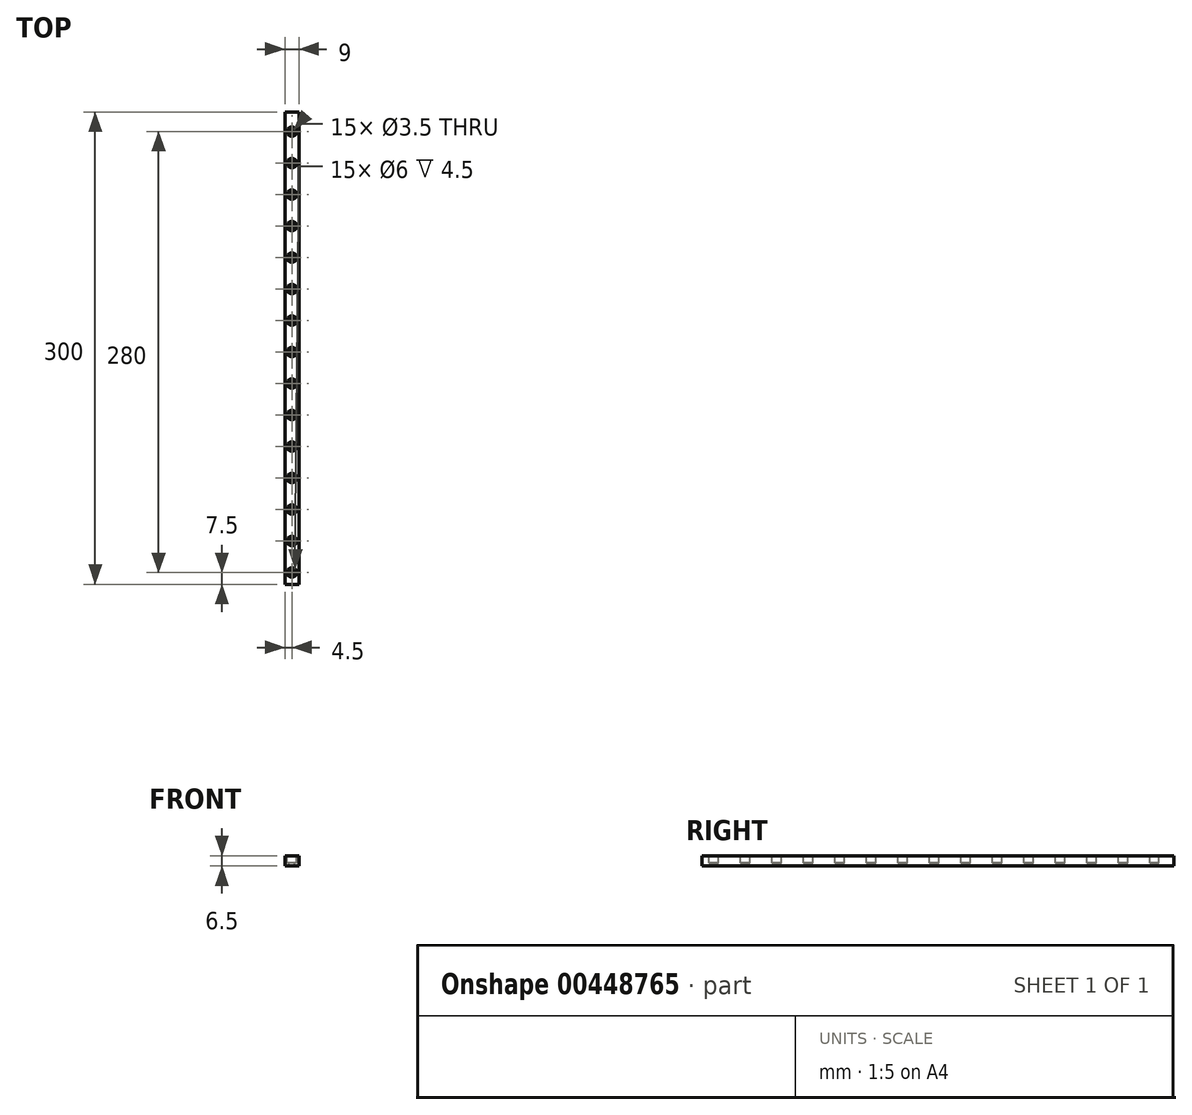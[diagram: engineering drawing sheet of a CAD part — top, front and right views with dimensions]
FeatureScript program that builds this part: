
annotation { "Feature Type Name" : "Feature", "Feature Type Description" : "" }
export const myFeature = defineFeature(function(context is Context, id is Id, definition is map)
    precondition{}
    {
        {
            var Q0;
            Q0=qCreatedBy(makeId("Front.planeOp"),FACE);
            var sketch = newSketch(context, id + "F0", { "sketchPlane" : qUnion([Q0])});
            skLineSegment(sketch, "E0.bottom", {"start": v(0, 0) * mm, "end": v(9, 0) * mm});
            skLineSegment(sketch, "E0.top", {"start": v(0, 6.5) * mm, "end": v(9, 6.5) * mm});
            skLineSegment(sketch, "E0.left", {"start": v(0, 0) * mm, "end": v(0, 6.5) * mm});
            skLineSegment(sketch, "E0.right", {"start": v(9, 0) * mm, "end": v(9, 6.5) * mm});
            skSolve(sketch);
        }
        {
            var Q0;
            Q0=qSketchRegion(id+"F0",true);
            extrude(context, id + "F1", {"entities" : qUnion([Q0]), "depth" : 300 * mm});
        }
        {
            var Q0;
            Q0=makeQuery(id+"F1.opExtrude","SWEPT_FACE",FACE,{"disambiguationData":[OSD([sQuery(id+"F0.wireOp",EDGE,"E0.top")])]});
            var sketch = newSketch(context, id + "F2", { "sketchPlane" : qUnion([Q0])});
            skPoint(sketch, "E1", {"position": v(4.5, -292.5) * mm});
            skPoint(sketch, "E1.positionSnap0", {"position": v(4.5, -300) * mm});
            skPoint(sketch, "E2.0.1.0", {"position": v(4.5, -272.5) * mm});
            skPoint(sketch, "E2.0.2.0", {"position": v(4.5, -252.5) * mm});
            skPoint(sketch, "E2.0.3.0", {"position": v(4.5, -232.5) * mm});
            skPoint(sketch, "E2.0.4.0", {"position": v(4.5, -212.5) * mm});
            skPoint(sketch, "E2.0.5.0", {"position": v(4.5, -192.5) * mm});
            skPoint(sketch, "E2.0.6.0", {"position": v(4.5, -172.5) * mm});
            skPoint(sketch, "E2.0.7.0", {"position": v(4.5, -152.5) * mm});
            skPoint(sketch, "E2.0.8.0", {"position": v(4.5, -132.5) * mm});
            skPoint(sketch, "E2.0.9.0", {"position": v(4.5, -112.5) * mm});
            skPoint(sketch, "E2.0.10.0", {"position": v(4.5, -92.5) * mm});
            skPoint(sketch, "E2.0.11.0", {"position": v(4.5, -72.5) * mm});
            skPoint(sketch, "E2.0.12.0", {"position": v(4.5, -52.5) * mm});
            skLineSegment(sketch, "E2.direction1", {"start": v(4.5, -292.5) * mm, "end": v(29.5, -292.5) * mm, "construction": true});
            skLineSegment(sketch, "E2.direction2", {"start": v(4.5, -292.5) * mm, "end": v(4.5, -272.5) * mm, "construction": true});
            skPoint(sketch, "E3.0.0.13", {"position": v(4.5, -32.5) * mm});
            skPoint(sketch, "E4.0.0.14", {"position": v(4.5, -12.5) * mm});
            skSolve(sketch);
        }
        {
            var Q0;
            Q0=sQuery(id+"F2.wireOp",VERTEX,"E1");
            var Q1;
            Q1=sQuery(id+"F2.wireOp",VERTEX,"E2.0.1.0");
            var Q2;
            Q2=sQuery(id+"F2.wireOp",VERTEX,"E2.0.2.0");
            var Q3;
            Q3=sQuery(id+"F2.wireOp",VERTEX,"E2.0.3.0");
            var Q4;
            Q4=sQuery(id+"F2.wireOp",VERTEX,"E2.0.4.0");
            var Q5;
            Q5=sQuery(id+"F2.wireOp",VERTEX,"E2.0.5.0");
            var Q6;
            Q6=sQuery(id+"F2.wireOp",VERTEX,"E2.0.6.0");
            var Q7;
            Q7=sQuery(id+"F2.wireOp",VERTEX,"E2.0.7.0");
            var Q8;
            Q8=sQuery(id+"F2.wireOp",VERTEX,"E2.0.8.0");
            var Q9;
            Q9=sQuery(id+"F2.wireOp",VERTEX,"E2.0.9.0");
            var Q10;
            Q10=sQuery(id+"F2.wireOp",VERTEX,"E2.0.10.0");
            var Q11;
            Q11=sQuery(id+"F2.wireOp",VERTEX,"E2.0.11.0");
            var Q12;
            Q12=sQuery(id+"F2.wireOp",VERTEX,"E2.0.12.0");
            var Q13;
            Q13=sQuery(id+"F2.wireOp",VERTEX,"E3.0.0.13");
            var Q14;
            Q14=sQuery(id+"F2.wireOp",VERTEX,"E4.0.0.14");
            var Q15;
            Q15=makeQuery(id+"F1.opExtrude","SWEPT_BODY",BODY,{"disambiguationData":[OSD([sQuery(id+"F0.wireOp",EDGE,"E0.bottom"),sQuery(id+"F0.wireOp",EDGE,"E0.top"),sQuery(id+"F0.wireOp",EDGE,"E0.left"),sQuery(id+"F0.wireOp",EDGE,"E0.right")])]});
            hole(context, id + "F3", {"style" : HoleStyle.C_BORE, "endStyle" : HoleEndStyle.THROUGH, "holeDiameter" : 3.5 * mm, "cBoreDiameter" : 6 * mm, "cBoreDepth" : 4.5 * mm, "locations" : qUnion([Q0, Q1, Q2, Q3, Q4, Q5, Q6, Q7, Q8, Q9, Q10, Q11, Q12, Q13, Q14]), "scope" : qUnion([Q15]), "isTappedThrough" : true});
        }
    });
